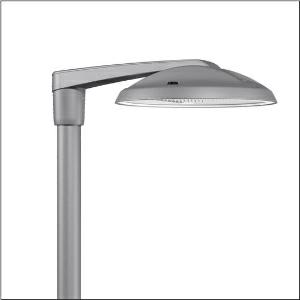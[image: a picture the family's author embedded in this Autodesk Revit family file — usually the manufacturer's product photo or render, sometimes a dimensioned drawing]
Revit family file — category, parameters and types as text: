
# Revit family: dl_r__50_iq_mini___st1_0a_5xa248d31v08me_e0eb
name_source: partatom
category: Lighting Fixtures
units: mm (PartAtom-declared; Revit-internal decimal feet)

## family parameters
Cut with Voids When Loaded = No
Host = Face
Light Source = No
Part Type = Normal
Room Calculation Point = No
Round Connector Dimension = Use Diameter
Shared = No

## types (1)
- --- (1 x LED, 15720 lm, 107 W, 3000K)
    Apparent Load = 107 VA
    CIE Flux Codes = 37 72 97 100 100
    Color Rendering = 70
    Color Temperature = 3000K
    Default Elevation = 1800 mm
    Description = DL® 50 iQ mini, mast luminaire, primary light control with lens, of PMMA, primary optical cover: cover, of toughened safety glass, transparent, light distribution: ST1.0a, light emission: direct distribution, primary light characteristic: asymmetric, installation type: post-top, side-entry, LED, High Power LED, rated luminous flux: 15.720lm, luminous efficacy: 147lm/W, light colour: 730, colour temperature: 3000K, control: optimised constant luminous flux control (CLO 2.0), Desk-Remote (wireless, voltage-free reading and setting of iQ features in the workshop via application-optimized NFC function/RFID function), Light-Fading, Smart-Wire, Night-Set, Lumen-Switch, Temp-Guard, Auto-Match, Street-Remote, presetting dimming logarithmic, mains connection: 230..240V, AC, 50/60Hz, connection cable pre-assembled, cable length: 10,5m, start of lifetime: 107W, end of service life: 113W, reduction: 47W, luminaire housing, of diecast aluminium, powder-coated, Siteco® metallic grey (DB 702S), inclination adjustable: 0°, 5°, 10° (post-top) | 0°, -5°, -10°, -15° (side-entry), please order mast post-top element or mast side-entry element separately, diameter: 500mm, height: 115mm, post-top: for spigot size d x l = 76 x 100mm; with reducer (optional accessory) 60 x 100mm | side-entry: for spigot size d x l = 60 x 100mm; with reducer (optional accessory) 42 x 100mm, Smart Interface above, protection rating (complete): IP66, insulation class (complete): insulation class II (safety insulation), certification: CE, ENEC, VDE, impact resistance: IK08, permissible operating ambient temperature for outdoor applications: -25..+40°C, standard-compliant lighting for roads and squares, packaging unit: 1 piece

Light Distribution: ST1.0a
    Height = 115 mm
    Lamp = 1 x LED
    Lamp Light Flux = 15720 lm
    Lamp Power = 107 W
    Lamp count = 1
    Length = 500 mm
    Luminous efficacy = 147 lm/W
    Manufacturer = Siteco
    ModVariant = No
    Model = 5XA248D31V08ME
    Number of Poles = 1
    OnlyDefault = Yes
    Power Factor = 1
    Product Name = DL® 50 iQ mini | ST1.0a
    Product group = mast luminaire | pylon top
    ProductGroupID = 6100
    Protection Class = Protection class II
    Protection Degree = IP 66
    RLX_Detail_Level = 1
    RLX_Emergency_Light_Flux = 0 lm
    RLX_Emergency_Type = 0
    RLX_Emergency_Type_DB = No
    RlxData = <blob elided: 106085 chars, md5=c246f4b0>
    Socket = socket
    Standby Power = 0 W
    System Light Flux = 15720 lm
    System Power = 107 W
    Type Comments = factory setting: luminous flux: 100 % | dim-lin: 254 | 565 mA
    Type Image = l_1251788.jpg
    URL = http://relux.com
    VarID = @adj_026245
    Voltage = 0 V
    Weight = 0.00 kg
    Width = 0 mm  [stored 0 ft]

note: [stored X ft] marks values corroborated as IEEE doubles in the binary element streams (Revit-internal decimal feet)

## geometry (parser evidence)
native form markers: Blend x4, Sweep x10
no freeform markers — native parametric forms only
